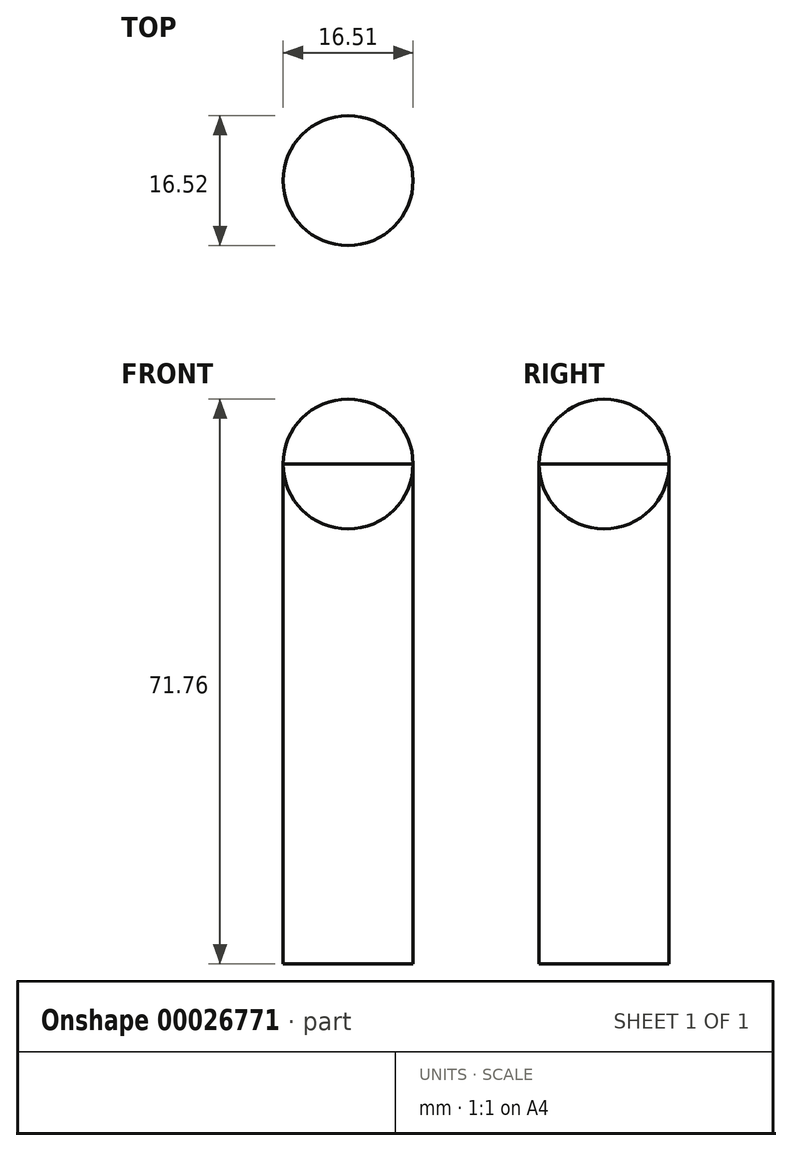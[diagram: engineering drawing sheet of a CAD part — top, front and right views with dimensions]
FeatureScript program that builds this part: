
annotation { "Feature Type Name" : "Feature", "Feature Type Description" : "" }
export const myFeature = defineFeature(function(context is Context, id is Id, definition is map)
    precondition{}
    {
        {
            var Q0;
            Q0=qCreatedBy(makeId("Front.planeOp"),FACE);
            var sketch = newSketch(context, id + "F0", { "sketchPlane" : qUnion([Q0])});
            skLineSegment(sketch, "E0.bottom", {"start": v(0, 52.5) * mm, "end": v(-8.26, 52.5) * mm});
            skLineSegment(sketch, "E0.top", {"start": v(0, -11) * mm, "end": v(-8.26, -11) * mm});
            skLineSegment(sketch, "E0.left", {"start": v(0, 52.5) * mm, "end": v(0, -11) * mm});
            skLineSegment(sketch, "E0.right", {"start": v(-8.26, 52.5) * mm, "end": v(-8.26, -11) * mm});
            skSolve(sketch);
        }
        {
            var Q0;
            Q0 = qSketchRegion(id + "F0", true);
            var Q1;
            Q1=sQuery(id+"F0.wireOp",EDGE,"E0.right");
            revolve(context, id + "F1", {"entities" : qUnion([Q0]), "axis" : qUnion([Q1]), "revolveType" : RevolveType.FULL});
        }
        {
            var Q0;
            Q0=makeQuery(id+"F1.opRevolve","SWEPT_FACE",FACE,{"disambiguationData":[OSD([sQuery(id+"F0.wireOp",EDGE,"E0.bottom")])]});
            var sketch = newSketch(context, id + "F2", { "sketchPlane" : qUnion([Q0])});
            skCircle(sketch, "E1", {"center": v(-8.26, 0) * mm, "radius": 8.26 * mm});
            skPoint(sketch, "E2", {"position": v(-8.26, 8.26) * mm});
            skPoint(sketch, "E3", {"position": v(-8.26, -8.26) * mm});
            skLineSegment(sketch, "E4", {"start": v(-8.26, 8.26) * mm, "end": v(-8.26, -8.26) * mm});
            skSolve(sketch);
        }
        {
            var Q0;
            {var subQ0=sQuery(id+"F2.wireOp",EDGE,"E4");Q0=makeQuery(id+"F2.imprint","IMPRINT",FACE,{"disambiguationData":[TD([[makeQuery(id+"F2.imprint","IMPRINT",EDGE,{"derivedFrom":subQ0}),1.0]])]});}
            var Q1;
            Q1=sQuery(id+"F2.wireOp",EDGE,"E4");
            revolve(context, id + "F3", {"entities" : qUnion([Q0]), "axis" : qUnion([Q1]), "revolveType" : RevolveType.FULL});
        }
    });
